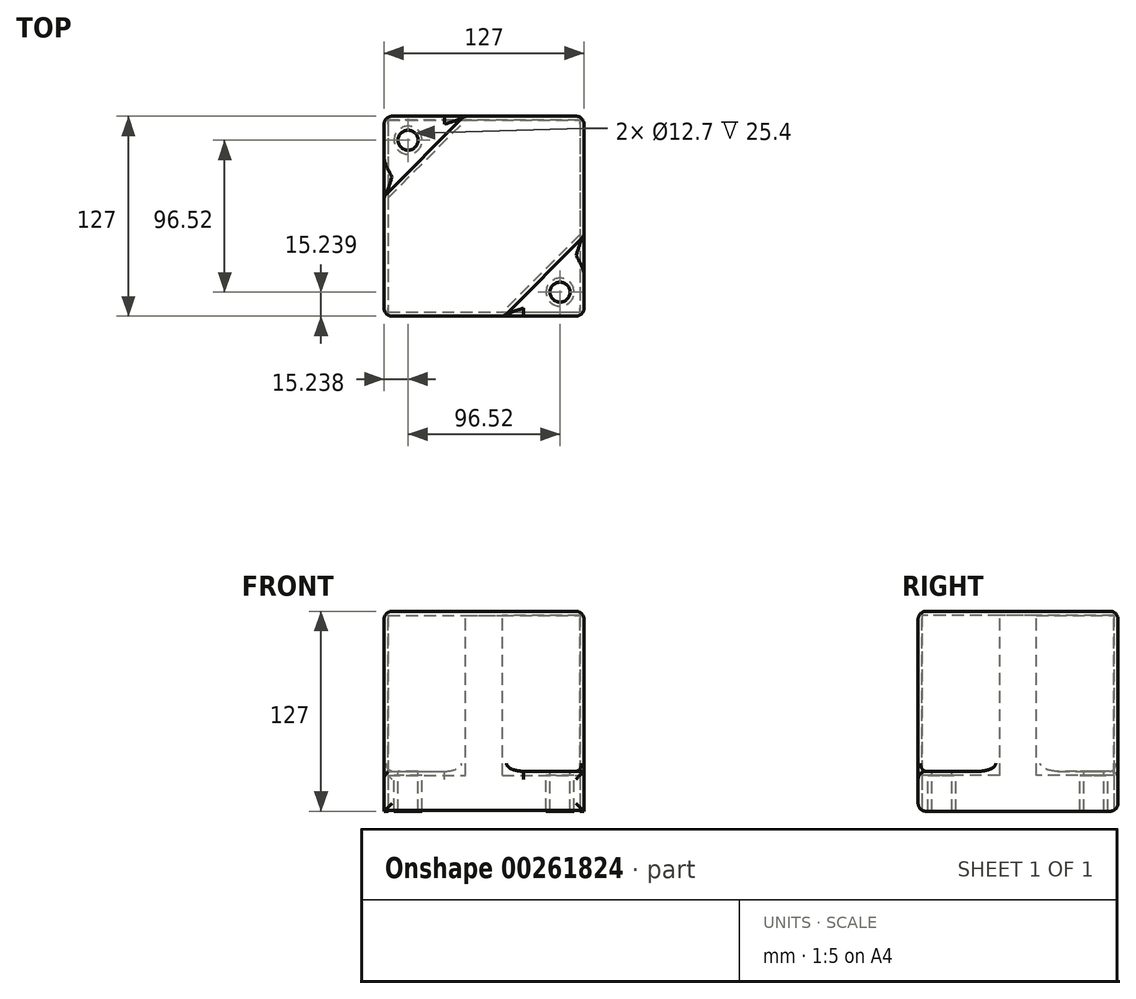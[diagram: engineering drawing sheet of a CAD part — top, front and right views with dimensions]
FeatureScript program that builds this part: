
annotation { "Feature Type Name" : "Feature", "Feature Type Description" : "" }
export const myFeature = defineFeature(function(context is Context, id is Id, definition is map)
    precondition{}
    {
        {
            var Q0;
            Q0=qCreatedBy(makeId("Top.planeOp"),FACE);
            var sketch = newSketch(context, id + "F0", { "sketchPlane" : qUnion([Q0])});
            skLineSegment(sketch, "E0.bottom", {"start": v(-63.5, 62.92) * mm, "end": v(63.5, 62.92) * mm});
            skLineSegment(sketch, "E0.top", {"start": v(-63.5, -64.08) * mm, "end": v(63.5, -64.08) * mm});
            skLineSegment(sketch, "E0.left", {"start": v(-63.5, 62.92) * mm, "end": v(-63.5, -64.08) * mm});
            skLineSegment(sketch, "E0.right", {"start": v(63.5, 62.92) * mm, "end": v(63.5, -64.08) * mm});
            skSolve(sketch);
        }
        {
            var Q0;
            Q0=makeQuery(id+"F0.imprint","IMPRINT",FACE,{"disambiguationData":[TD([[makeQuery(id+"F0.imprint","IMPRINT",EDGE,{"derivedFrom":sQuery(id+"F0.wireOp",EDGE,"E0.bottom")}),-1.0]])]});
            extrude(context, id + "F1", {"entities" : qUnion([Q0]), "depth" : 127 * mm});
        }
        {
            var Q0;
            Q0=makeQuery(id+"F1.opExtrude","CAP_FACE",FACE,{"disambiguationData":[OSD([sQuery(id+"F0.wireOp",EDGE,"E0.bottom"),sQuery(id+"F0.wireOp",EDGE,"E0.top"),sQuery(id+"F0.wireOp",EDGE,"E0.left"),sQuery(id+"F0.wireOp",EDGE,"E0.right")])],"isStart":false});
            var sketch = newSketch(context, id + "F2", { "sketchPlane" : qUnion([Q0])});
            skLineSegment(sketch, "E1", {"start": v(-63.5, -64.08) * mm, "end": v(63.5, 62.92) * mm, "construction": true});
            skLineSegment(sketch, "E2", {"start": v(-63.5, 12.12) * mm, "end": v(-12.7, 62.92) * mm});
            skLineSegment(sketch, "E3", {"start": v(-63.5, 62.92) * mm, "end": v(-63.5, 12.12) * mm});
            skLineSegment(sketch, "E4", {"start": v(-63.5, 62.92) * mm, "end": v(-12.7, 62.92) * mm});
            skSolve(sketch);
        }
        {
            var Q0;
            Q0=makeQuery(id+"F2.imprint","IMPRINT",FACE,{"disambiguationData":[TD([[makeQuery(id+"F2.imprint","IMPRINT",EDGE,{"derivedFrom":sQuery(id+"F2.wireOp",EDGE,"E2")}),1.0]])]});
            extrude(context, id + "F3", {"entities" : qUnion([Q0]), "operationType" : NewBodyOperationType.REMOVE, "oppositeDirection" : true, "depth" : 101.6 * mm});
        }
        {
            var Q0;
            Q0=makeQuery(id+"F1.opExtrude","CAP_FACE",FACE,{"disambiguationData":[OSD([sQuery(id+"F0.wireOp",EDGE,"E0.bottom"),sQuery(id+"F0.wireOp",EDGE,"E0.top"),sQuery(id+"F0.wireOp",EDGE,"E0.left"),sQuery(id+"F0.wireOp",EDGE,"E0.right")])],"isStart":false});
            var sketch = newSketch(context, id + "F4", { "sketchPlane" : qUnion([Q0])});
            skLineSegment(sketch, "E5", {"start": v(63.5, -64.08) * mm, "end": v(63.5, -13.28) * mm});
            skLineSegment(sketch, "E6", {"start": v(63.5, -13.28) * mm, "end": v(12.7, -64.08) * mm});
            skLineSegment(sketch, "E7", {"start": v(12.7, -64.08) * mm, "end": v(63.5, -64.08) * mm});
            skSolve(sketch);
        }
        {
            var Q0;
            Q0=makeQuery(id+"F4.imprint","IMPRINT",FACE,{"disambiguationData":[TD([[makeQuery(id+"F4.imprint","IMPRINT",EDGE,{"derivedFrom":sQuery(id+"F4.wireOp",EDGE,"E5")}),-1.0]])]});
            extrude(context, id + "F5", {"entities" : qUnion([Q0]), "operationType" : NewBodyOperationType.REMOVE, "oppositeDirection" : true, "depth" : 101.6 * mm});
        }
        {
            var Q0;
            Q0=makeQuery(id+"F3.boolean.opBoolean","COPY",FACE,{"derivedFrom":makeQuery(id+"F3.opExtrude","CAP_FACE",FACE,{"disambiguationData":[OSD([sQuery(id+"F2.wireOp",EDGE,"E2"),sQuery(id+"F2.wireOp",EDGE,"E3"),sQuery(id+"F2.wireOp",EDGE,"E4")])],"isStart":false})});
            var sketch = newSketch(context, id + "F6", { "sketchPlane" : qUnion([Q0])});
            skCircle(sketch, "E8", {"center": v(-48.26, 47.68) * mm, "radius": 6.35 * mm});
            skSolve(sketch);
        }
        {
            var Q0;
            Q0=makeQuery(id+"F5.boolean.opBoolean","COPY",FACE,{"derivedFrom":makeQuery(id+"F5.opExtrude","CAP_FACE",FACE,{"disambiguationData":[OSD([sQuery(id+"F4.wireOp",EDGE,"E5"),sQuery(id+"F4.wireOp",EDGE,"E6"),sQuery(id+"F4.wireOp",EDGE,"E7")])],"isStart":false})});
            var sketch = newSketch(context, id + "F7", { "sketchPlane" : qUnion([Q0])});
            skCircle(sketch, "E9", {"center": v(48.26, -48.84) * mm, "radius": 6.35 * mm});
            skSolve(sketch);
        }
        {
            var Q0;
            Q0=makeQuery(id+"F6.imprint","IMPRINT",FACE,{"disambiguationData":[TD([[makeQuery(id+"F6.imprint","IMPRINT",EDGE,{"derivedFrom":sQuery(id+"F6.wireOp",EDGE,"E8")}),1.0]])]});
            var Q1;
            Q1=makeQuery(id+"F7.imprint","IMPRINT",FACE,{"disambiguationData":[TD([[makeQuery(id+"F7.imprint","IMPRINT",EDGE,{"derivedFrom":sQuery(id+"F7.wireOp",EDGE,"E9")}),1.0]])]});
            extrude(context, id + "F8", {"entities" : qUnion([Q0, Q1]), "operationType" : NewBodyOperationType.REMOVE, "oppositeDirection" : true, "depth" : 203.2 * mm});
        }
        {
            var Q0;
            Q0=makeQuery(id+"F1.opExtrude","CAP_FACE",FACE,{"disambiguationData":[OSD([sQuery(id+"F0.wireOp",EDGE,"E0.bottom"),sQuery(id+"F0.wireOp",EDGE,"E0.top"),sQuery(id+"F0.wireOp",EDGE,"E0.left"),sQuery(id+"F0.wireOp",EDGE,"E0.right")])],"isStart":true});
            shell(context, id + "F9", {"entities" : qUnion([Q0]), "thickness" : 2.54 * mm});
        }
        {
            var Q0;
            Q0=makeQuery(id+"F1.opExtrude","CAP_FACE",FACE,{"disambiguationData":[OSD([sQuery(id+"F0.wireOp",EDGE,"E0.bottom"),sQuery(id+"F0.wireOp",EDGE,"E0.top"),sQuery(id+"F0.wireOp",EDGE,"E0.left"),sQuery(id+"F0.wireOp",EDGE,"E0.right")])],"isStart":false});
            var Q1;
            Q1=makeQuery(id+"F1.opExtrude","SWEPT_FACE",FACE,{"disambiguationData":[OSD([sQuery(id+"F0.wireOp",EDGE,"E0.bottom")])]});
            var Q2;
            Q2=makeQuery(id+"F3.boolean.opBoolean","COPY",FACE,{"derivedFrom":makeQuery(id+"F3.opExtrude","SWEPT_FACE",FACE,{"disambiguationData":[OSD([sQuery(id+"F2.wireOp",EDGE,"E2")])]})});
            var Q3;
            Q3=makeQuery(id+"F1.opExtrude","SWEPT_FACE",FACE,{"disambiguationData":[OSD([sQuery(id+"F0.wireOp",EDGE,"E0.top")])]});
            var Q4;
            Q4=makeQuery(id+"F5.boolean.opBoolean","COPY",FACE,{"derivedFrom":makeQuery(id+"F5.opExtrude","SWEPT_FACE",FACE,{"disambiguationData":[OSD([sQuery(id+"F4.wireOp",EDGE,"E6")])]})});
            fillet(context, id + "F10", {"entities" : qUnion([Q0, Q1, Q2, Q3, Q4]), "radius" : 5.08 * mm, "tangentPropagation" : true, "allowEdgeOverflow" : false});
        }
    });
